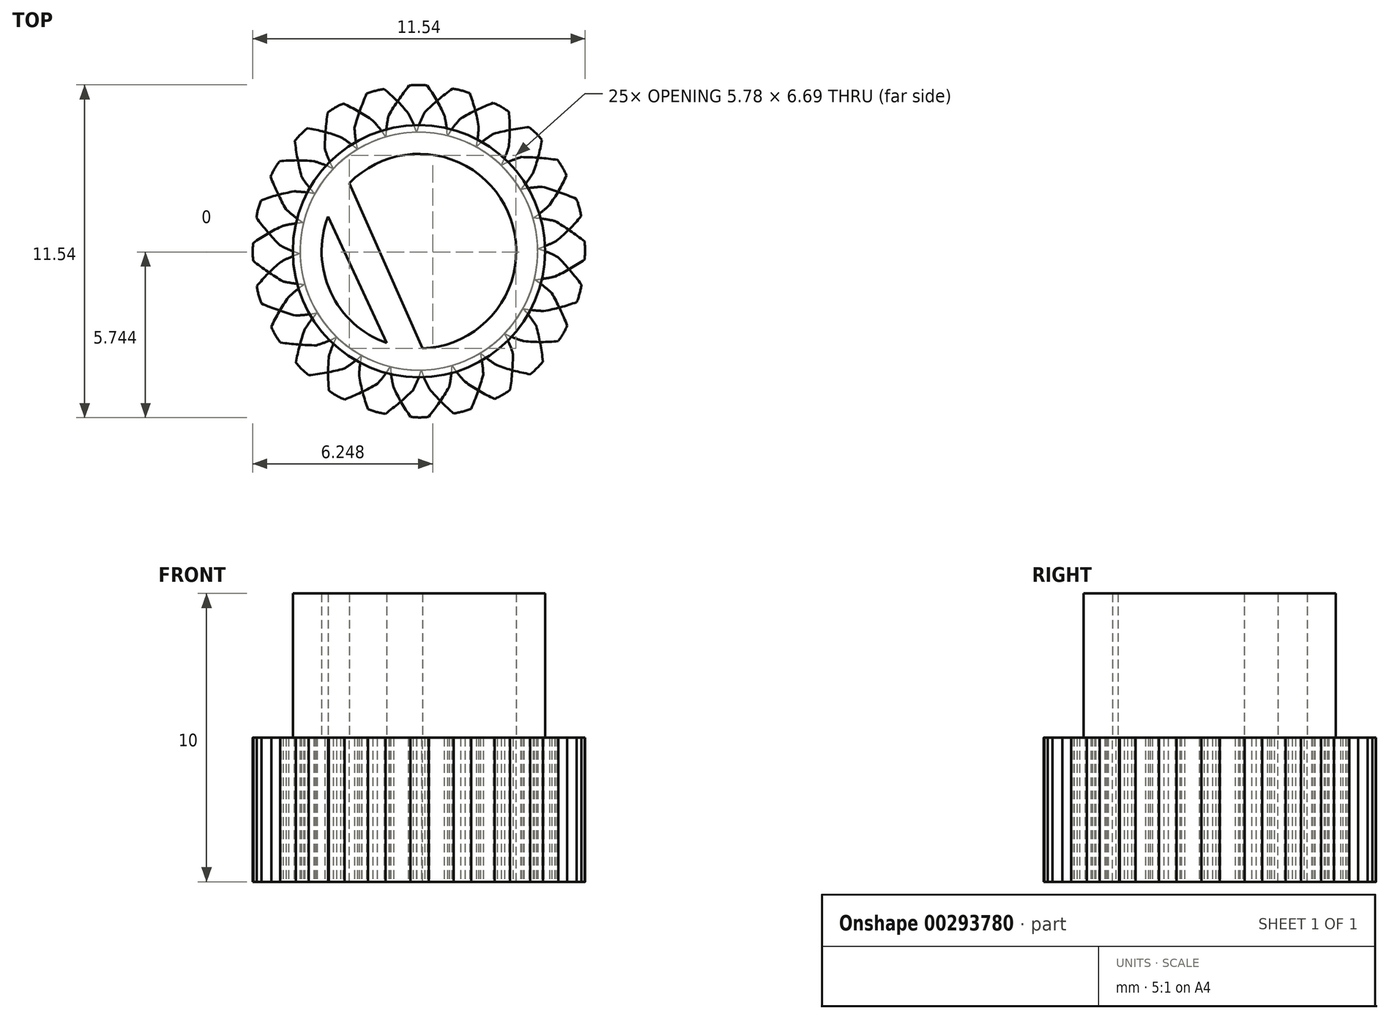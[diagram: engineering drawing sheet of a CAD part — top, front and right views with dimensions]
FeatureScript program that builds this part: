
annotation { "Feature Type Name" : "Feature", "Feature Type Description" : "" }
export const myFeature = defineFeature(function(context is Context, id is Id, definition is map)
    precondition{}
    {
        {
            var Q0;
            Q0=qCreatedBy(makeId("Top.planeOp"),FACE);
            var sketch = newSketch(context, id + "F0", { "sketchPlane" : qUnion([Q0])});
            skCircle(sketch, "E0", {"center": v(0, 0) * mm, "radius": 4.63 * mm, "construction": true});
            skCircle(sketch, "E1", {"center": v(0, 0) * mm, "radius": 4.12 * mm});
            skCircle(sketch, "E2", {"center": v(0, 0) * mm, "radius": 5.12 * mm, "construction": true});
            skLineSegment(sketch, "E3", {"start": v(0, 0) * mm, "end": v(0, 5.12) * mm, "construction": true});
            skLineSegment(sketch, "E4", {"start": v(0, 13) * mm, "end": v(-1, 13) * mm, "construction": true});
            skLineSegment(sketch, "E5", {"start": v(0, 13) * mm, "end": v(1, 13) * mm, "construction": true});
            skArc(sketch, "E6", {"start": v(0.39, 13) * mm, "mid": v(0.25, 13) * mm, "end": v(0.12, 13) * mm});
            skArc(sketch, "E7", {"start": v(0, 5.06) * mm, "mid": v(0, 5.07) * mm, "end": v(0, 5.07) * mm});
            skArc(sketch, "E8.trimOffspring", {"start": v(-0.12, 13) * mm, "mid": v(-0.25, 13) * mm, "end": v(-0.38, 13) * mm});
            skLineSegment(sketch, "E9.trimOffspring", {"start": v(0, 5.07) * mm, "end": v(0, 117.25) * mm, "construction": true});
            skPoint(sketch, "E10.start.orphan", {"position": v(1.02, 3.76) * mm});
            skPoint(sketch, "E11.start.orphan", {"position": v(1.02, 3.84) * mm});
            skArc(sketch, "E12", {"start": v(0.3, 4.62) * mm, "mid": v(0.29, 4.63) * mm, "end": v(0.28, 4.65) * mm});
            skArc(sketch, "E13.trimOffspring", {"start": v(-0.3, 4.65) * mm, "mid": v(-0.3, 4.63) * mm, "end": v(-0.3, 4.61) * mm});
            skArc(sketch, "E14.trimOffspring", {"start": v(-0.4, 3.6) * mm, "mid": v(-0.4, 3.6) * mm, "end": v(-0.4, 3.6) * mm});
            skArc(sketch, "E15", {"start": v(1.05, 12.96) * mm, "mid": v(1.03, 13.49) * mm, "end": v(0.94, 14.01) * mm});
            skArc(sketch, "E16.trimOffspring", {"start": v(-0.99, 14.01) * mm, "mid": v(-1.07, 13.49) * mm, "end": v(-1.1, 12.96) * mm});
            skArc(sketch, "E17", {"start": v(0.94, 14.01) * mm, "mid": v(0.67, 14.54) * mm, "end": v(0.35, 15.04) * mm});
            skArc(sketch, "E18", {"start": v(0.35, 15.04) * mm, "mid": v(0.03, 15.06) * mm, "end": v(-0.28, 15.04) * mm});
            skArc(sketch, "E19.trimOffspring", {"start": v(-0.28, 15.04) * mm, "mid": v(-0.65, 14.54) * mm, "end": v(-0.99, 14.01) * mm});
            skArc(sketch, "E20", {"start": v(1, 3.66) * mm, "mid": v(0.97, 4.2) * mm, "end": v(0.88, 4.72) * mm});
            skArc(sketch, "E21.trimOffspring", {"start": v(-1.05, 4.72) * mm, "mid": v(-1.13, 4.2) * mm, "end": v(-1.15, 3.66) * mm});
            skArc(sketch, "E22", {"start": v(0.88, 4.72) * mm, "mid": v(0.6, 5.25) * mm, "end": v(0.29, 5.75) * mm});
            skArc(sketch, "E23", {"start": v(0.29, 5.75) * mm, "mid": v(-0.03, 5.77) * mm, "end": v(-0.34, 5.75) * mm});
            skArc(sketch, "E24.trimOffspring", {"start": v(-0.34, 5.75) * mm, "mid": v(-0.71, 5.24) * mm, "end": v(-1.05, 4.72) * mm});
            skArc(sketch, "E25", {"start": v(-0.45, 4.6) * mm, "mid": v(-0.53, 4.35) * mm, "end": v(-0.6, 4.08) * mm});
            skArc(sketch, "E26", {"start": v(-0.19, 5.12) * mm, "mid": v(-0.36, 4.88) * mm, "end": v(-0.45, 4.6) * mm});
            skSolve(sketch);
        }
        {
            var Q0;
            Q0=qSketchRegion(id+"F0",true);
            extrude(context, id + "F1", {"entities" : qUnion([Q0]), "depth" : 5 * mm});
        }
        {
            var Q0;
            Q0=makeQuery(id+"F1.opExtrude","SWEPT_BODY",BODY,{"disambiguationData":[OSD([sQuery(id+"F0.wireOp",EDGE,"E1"),sQuery(id+"F0.wireOp",EDGE,"E6"),sQuery(id+"F0.wireOp",EDGE,"8135d3ed-eb66-4b9b-a605-aa948f9b6877.trimOffspring"),sQuery(id+"F0.wireOp",EDGE,"E7"),sQuery(id+"F0.wireOp",EDGE,"NEc80oSd-jkKK-Rj08-4cXk-I9QzhTEvkPhy"),sQuery(id+"F0.wireOp",EDGE,"69d1582d-723c-4c18-846d-3caa5e789cbb.trimOffspring")])]});
            var Q1;
            Q1=makeQuery(id+"F1.opExtrude","SWEPT_FACE",FACE,{"disambiguationData":[OSD([sQuery(id+"F0.wireOp",EDGE,"E1")])]});
            circularPattern(context, id + "F2", {"entities" : qUnion([Q0]), "axis" : qUnion([Q1]), "angle" : 360 * degree, "instanceCount" : 24, "equalSpace" : true});
        }
        {
            var Q0;
            Q0=makeQuery(id+"F1.opExtrude","CAP_FACE",FACE,{"disambiguationData":[OSD([sQuery(id+"F0.wireOp",EDGE,"E1"),sQuery(id+"F0.wireOp",EDGE,"E6"),sQuery(id+"F0.wireOp",EDGE,"8135d3ed-eb66-4b9b-a605-aa948f9b6877.trimOffspring"),sQuery(id+"F0.wireOp",EDGE,"E7"),sQuery(id+"F0.wireOp",EDGE,"NEc80oSd-jkKK-Rj08-4cXk-I9QzhTEvkPhy"),sQuery(id+"F0.wireOp",EDGE,"69d1582d-723c-4c18-846d-3caa5e789cbb.trimOffspring")])],"isStart":false});
            var sketch = newSketch(context, id + "F3", { "sketchPlane" : qUnion([Q0])});
            skPoint(sketch, "E27.middle", {"position": v(0, 0) * mm});
            skPoint(sketch, "E27.right.end.orphan", {"position": v(-2.12, 2.12) * mm});
            skPoint(sketch, "E28.right.end.orphan", {"position": v(-3.33, 3.33) * mm});
            skPoint(sketch, "E27.bottom.end.orphan", {"position": v(-2.12, -2.12) * mm});
            skPoint(sketch, "E27.left.end.orphan", {"position": v(2.12, 2.12) * mm});
            skPoint(sketch, "E27.left.start.orphan", {"position": v(2.12, -2.12) * mm});
            skPoint(sketch, "E28.left.end.orphan", {"position": v(3.33, 3.33) * mm});
            skPoint(sketch, "E28.bottom.end.orphan", {"position": v(-3.33, -3.33) * mm});
            skPoint(sketch, "E28.bottom.start.orphan", {"position": v(3.33, -3.33) * mm});
            skArc(sketch, "E29", {"start": v(-3.37, 0.06) * mm, "mid": v(-3.37, 0.03) * mm, "end": v(-3.38, 0) * mm});
            skLineSegment(sketch, "E30", {"start": v(0, 3.38) * mm, "end": v(0, 3.62) * mm});
            skLineSegment(sketch, "E31", {"start": v(0, 0) * mm, "end": v(0, 0.25) * mm});
            skCircle(sketch, "E32", {"center": v(0, 0) * mm, "radius": 3.38 * mm});
            skPoint(sketch, "E33.orphan", {"position": v(0, 4) * mm});
            skLineSegment(sketch, "E34", {"start": v(-2.41, 2.36) * mm, "end": v(0.12, -3.37) * mm});
            skPoint(sketch, "E35.start.orphan", {"position": v(0, -3.38) * mm});
            skPoint(sketch, "E36.orphan", {"position": v(3.38, 0) * mm});
            skLineSegment(sketch, "E37", {"start": v(0, 3.38) * mm, "end": v(0, 4) * mm});
            skLineSegment(sketch, "E38", {"start": v(0.12, -3.37) * mm, "end": v(0.12, -4.12) * mm});
            skSolve(sketch);
        }
        {
            var Q0;
            {var subQ0=sQuery(id+"F3.wireOp",EDGE,"E35");Q0=makeQuery(id+"F3.imprint","IMPRINT",FACE,{"disambiguationData":[TD([[makeQuery(id+"F3.imprint","IMPRINT",EDGE,{"derivedFrom":subQ0}),-1.0]])]});}
            var Q1;
            {var subQ2=sQuery(id+"F3.wireOp",EDGE,"E34");Q1=makeQuery(id+"F3.imprint","IMPRINT",FACE,{"disambiguationData":[TD([[makeQuery(id+"F3.imprint","IMPRINT",EDGE,{"derivedFrom":subQ2}),1.0]])]});}
            extrude(context, id + "F4", {"entities" : qUnion([Q0, Q1]), "operationType" : NewBodyOperationType.REMOVE, "oppositeDirection" : true, "depth" : 25 * mm});
        }
        {
            var Q0;
            Q0=makeQuery(id+"F2.opPattern","COPY",FACE,{"derivedFrom":makeQuery(id+"F1.opExtrude","CAP_FACE",FACE,{"disambiguationData":[OSD([sQuery(id+"F0.wireOp",EDGE,"E1"),sQuery(id+"F0.wireOp",EDGE,"ce9dac7b-c6a7-4aa2-8854-a52381f8a8e8"),sQuery(id+"F0.wireOp",EDGE,"06ce8aa9-c749-40ed-9192-5f1dd213df4d.trimOffspring"),sQuery(id+"F0.wireOp",EDGE,"f63a663b-90d1-4972-b024-fb19c3c43451"),sQuery(id+"F0.wireOp",EDGE,"90c57f24-a5db-4b47-97ce-a6af5debadce"),sQuery(id+"F0.wireOp",EDGE,"e15c1dc4-cf10-48a9-8e95-0bd51a33337e.trimOffspring")])],"isStart":false}),"instanceName":"9"});
            var sketch = newSketch(context, id + "F5", { "sketchPlane" : qUnion([Q0])});
            skPoint(sketch, "E39.start.orphan", {"position": v(-2.22, 2.54) * mm});
            skPoint(sketch, "E40.start.orphan", {"position": v(-3.25, 2.54) * mm});
            skCircle(sketch, "E41", {"center": v(0, 0) * mm, "radius": 3.38 * mm});
            skCircle(sketch, "E42", {"center": v(0, 0) * mm, "radius": 4.38 * mm});
            skLineSegment(sketch, "E43", {"start": v(-0.59, -4.34) * mm, "end": v(-3.7, 2.35) * mm});
            skSolve(sketch);
        }
        {
            var Q0;
            Q0=qSketchRegion(id+"F5",true);
            var Q1;
            {var subQ0=sQuery(id+"F5.wireOp",EDGE,"E40");var subQ1=sQuery(id+"F5.wireOp",EDGE,"pEozFyju-i5PG-pIGt-Xkxd-JWm3oXukfSJh");var subQ2=makeQuery(id+"F5.imprint","INTERSECT",VERTEX,{"disambiguationData":[OD(0.0)],"derivedFrom":[subQ1,subQ0]});Q1=makeQuery(id+"F5.imprint","IMPRINT",FACE,{"disambiguationData":[TD([[makeQuery(id+"F5.imprint","IMPRINT",EDGE,{"disambiguationData":[TD([[subQ2,-1.0]])],"derivedFrom":subQ1}),1.0]])]});}
            var Q2;
            {var subQ0=sQuery(id+"F5.wireOp",EDGE,"E39");Q2=makeQuery(id+"F5.imprint","IMPRINT",FACE,{"disambiguationData":[TD([[makeQuery(id+"F5.imprint","IMPRINT",EDGE,{"derivedFrom":subQ0}),1.0]])]});}
            var Q3;
            {var subQ0=sQuery(id+"F5.wireOp",EDGE,"E43");var subQ1=sQuery(id+"F5.wireOp",EDGE,"E41");var subQ2=makeQuery(id+"F5.imprint","INTERSECT",VERTEX,{"disambiguationData":[OD(0.0)],"derivedFrom":[subQ1,subQ0]});Q3=makeQuery(id+"F5.imprint","IMPRINT",FACE,{"disambiguationData":[TD([[makeQuery(id+"F5.imprint","IMPRINT",EDGE,{"disambiguationData":[TD([[subQ2,1.0]])],"derivedFrom":subQ0}),-1.0]])]});}
            var Q4;
            {var subQ0=sQuery(id+"F5.wireOp",EDGE,"E43");var subQ1=sQuery(id+"F5.wireOp",EDGE,"E41");var subQ2=makeQuery(id+"F5.imprint","INTERSECT",VERTEX,{"disambiguationData":[OD(0.0)],"derivedFrom":[subQ1,subQ0]});Q4=makeQuery(id+"F5.imprint","IMPRINT",FACE,{"disambiguationData":[TD([[makeQuery(id+"F5.imprint","IMPRINT",EDGE,{"disambiguationData":[TD([[subQ2,-1.0]])],"derivedFrom":subQ1}),1.0]])]});}
            extrude(context, id + "F6", {"entities" : qUnion([Q0, Q1, Q2, Q3, Q4]), "depth" : 5 * mm});
        }
    });
